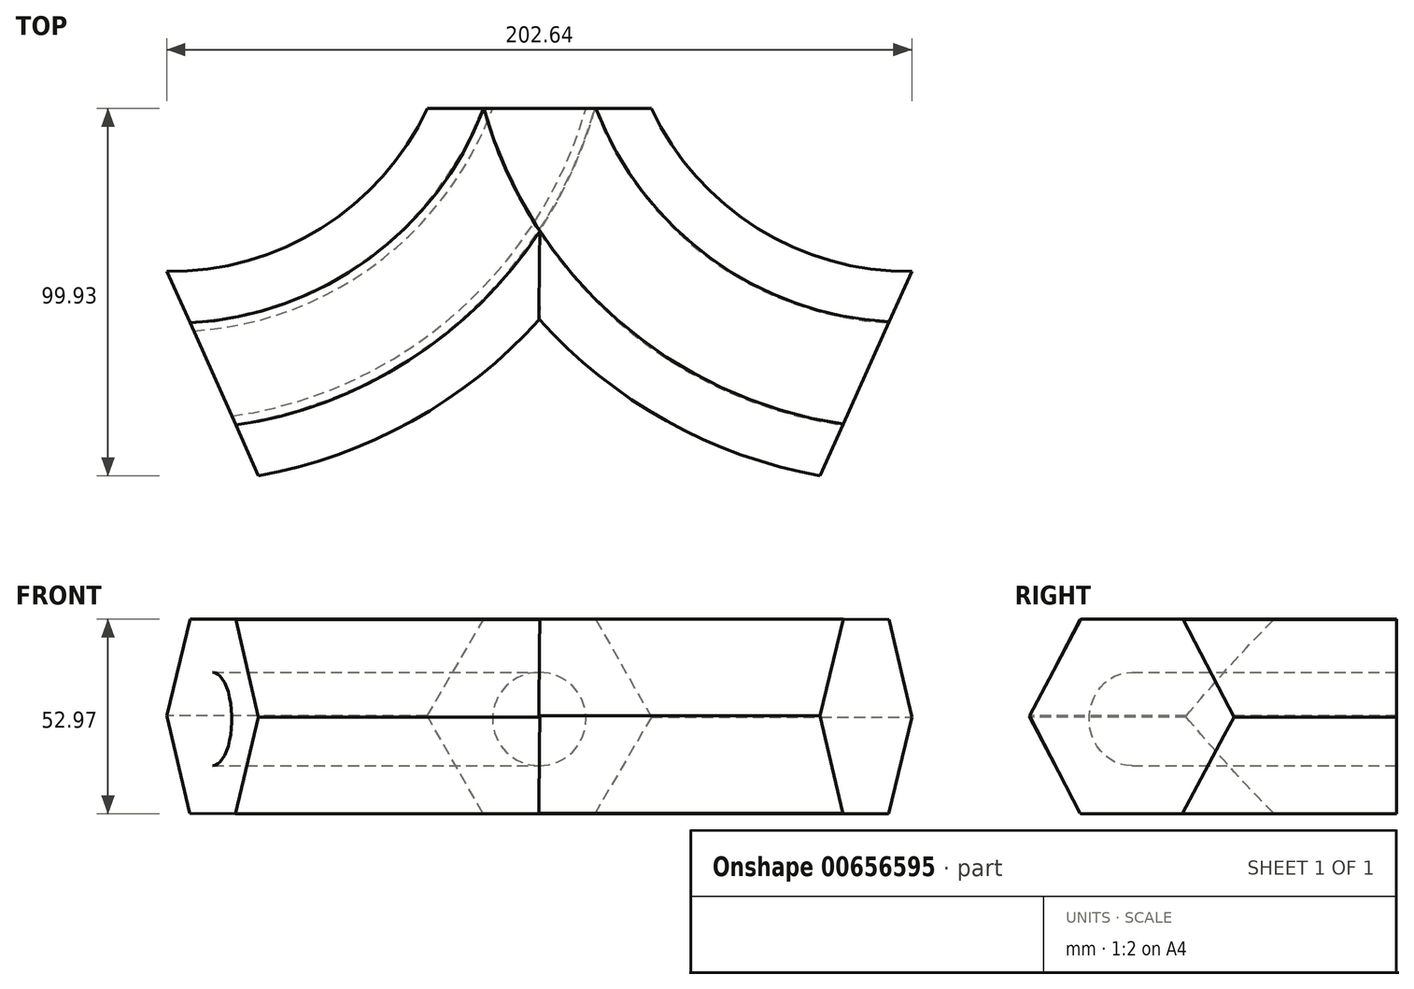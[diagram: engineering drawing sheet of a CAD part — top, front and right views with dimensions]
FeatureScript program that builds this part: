
annotation { "Feature Type Name" : "Feature", "Feature Type Description" : "" }
export const myFeature = defineFeature(function(context is Context, id is Id, definition is map)
    precondition{}
    {
        {
            var Q0;
            Q0=qCreatedBy(makeId("Front.planeOp"),FACE);
            var sketch = newSketch(context, id + "F0", { "sketchPlane" : qUnion([Q0])});
            skCircle(sketch, "E0.cCircle", {"center": v(0, 26.89) * mm, "radius": 26.4 * mm, "construction": true});
            skLineSegment(sketch, "E0.0", {"start": v(-15.4, 0.58) * mm, "end": v(-30.48, 27.07) * mm});
            skLineSegment(sketch, "E0.1", {"start": v(-30.48, 27.07) * mm, "end": v(-15.08, 53.37) * mm});
            skLineSegment(sketch, "E0.2", {"start": v(-15.08, 53.37) * mm, "end": v(15.4, 53.2) * mm});
            skLineSegment(sketch, "E0.3", {"start": v(15.4, 53.2) * mm, "end": v(30.48, 26.7) * mm});
            skLineSegment(sketch, "E0.4", {"start": v(30.48, 26.7) * mm, "end": v(15.08, 0.4) * mm});
            skLineSegment(sketch, "E0.5", {"start": v(15.08, 0.4) * mm, "end": v(-15.4, 0.58) * mm});
            skPoint(sketch, "E0.0.midPoint", {"position": v(-22.94, 13.82) * mm});
            skSolve(sketch);
        }
        {
            var Q0;
            Q0=qCreatedBy(makeId("Top.planeOp"),FACE);
            var sketch = newSketch(context, id + "F1", { "sketchPlane" : qUnion([Q0])});
            skArc(sketch, "E1", {"start": v(-88.86, -72.11) * mm, "mid": v(-33.77, -49.2) * mm, "end": v(0, 0) * mm});
            skArc(sketch, "E2.MirrorCS", {"start": v(88.86, -72.11) * mm, "mid": v(33.77, -49.2) * mm, "end": v(0, 0) * mm});
            skSolve(sketch);
        }
        {
            var Q0;
            Q0=makeQuery(id+"F0.imprint","IMPRINT",FACE,{"disambiguationData":[TD([[makeQuery(id+"F0.imprint","IMPRINT",EDGE,{"derivedFrom":sQuery(id+"F0.wireOp",EDGE,"E0.0")}),-1.0]])]});
            var Q1;
            Q1=sQuery(id+"F1.wireOp",EDGE,"E2.MirrorCS");
            sweep(context, id + "F2", {"profiles" : qUnion([Q0]), "path" : qUnion([Q1])});
        }
        {
            var Q0;
            Q0=makeQuery(id+"F0.imprint","IMPRINT",FACE,{"disambiguationData":[TD([[makeQuery(id+"F0.imprint","IMPRINT",EDGE,{"derivedFrom":sQuery(id+"F0.wireOp",EDGE,"E0.0")}),-1.0]])]});
            var Q1;
            Q1=sQuery(id+"F1.wireOp",EDGE,"E1");
            sweep(context, id + "F3", {"operationType" : NewBodyOperationType.ADD, "profiles" : qUnion([Q0]), "path" : qUnion([Q1])});
        }
        {
            var Q0;
            Q0=makeQuery(id+"F0.imprint","IMPRINT",FACE,{"disambiguationData":[TD([[makeQuery(id+"F0.imprint","IMPRINT",EDGE,{"derivedFrom":sQuery(id+"F0.wireOp",EDGE,"E0.0")}),-1.0]])]});
            var sketch = newSketch(context, id + "F4", { "sketchPlane" : qUnion([Q0])});
            skLineSegment(sketch, "E3", {"start": v(0, 0) * mm, "end": v(0, 52.37) * mm});
            skPoint(sketch, "E4", {"position": v(0, 26.18) * mm});
            skCircle(sketch, "E5", {"center": v(0, 26.18) * mm, "radius": 12.7 * mm});
            skSolve(sketch);
        }
        {
            var Q0;
            {var subQ0=sQuery(id+"F4.wireOp",EDGE,"E5");var subQ1=sQuery(id+"F4.wireOp",EDGE,"E3");var subQ2=makeQuery(id+"F4.imprint","INTERSECT",VERTEX,{"disambiguationData":[OD(0.0)],"derivedFrom":[subQ1,subQ0]});Q0=makeQuery(id+"F4.imprint","IMPRINT",FACE,{"disambiguationData":[TD([[makeQuery(id+"F4.imprint","IMPRINT",EDGE,{"disambiguationData":[TD([[subQ2,-1.0]])],"derivedFrom":subQ1}),-1.0]])]});}
            var Q1;
            {var subQ0=sQuery(id+"F4.wireOp",EDGE,"E5");var subQ1=sQuery(id+"F4.wireOp",EDGE,"E3");var subQ2=makeQuery(id+"F4.imprint","INTERSECT",VERTEX,{"disambiguationData":[OD(0.0)],"derivedFrom":[subQ1,subQ0]});Q1=makeQuery(id+"F4.imprint","IMPRINT",FACE,{"disambiguationData":[TD([[makeQuery(id+"F4.imprint","IMPRINT",EDGE,{"disambiguationData":[TD([[subQ2,-1.0]])],"derivedFrom":subQ1}),1.0]])]});}
            var Q2;
            Q2=sQuery(id+"F1.wireOp",EDGE,"E1");
            sweep(context, id + "F5", {"operationType" : NewBodyOperationType.REMOVE, "profiles" : qUnion([Q0, Q1]), "path" : qUnion([Q2])});
        }
    });
